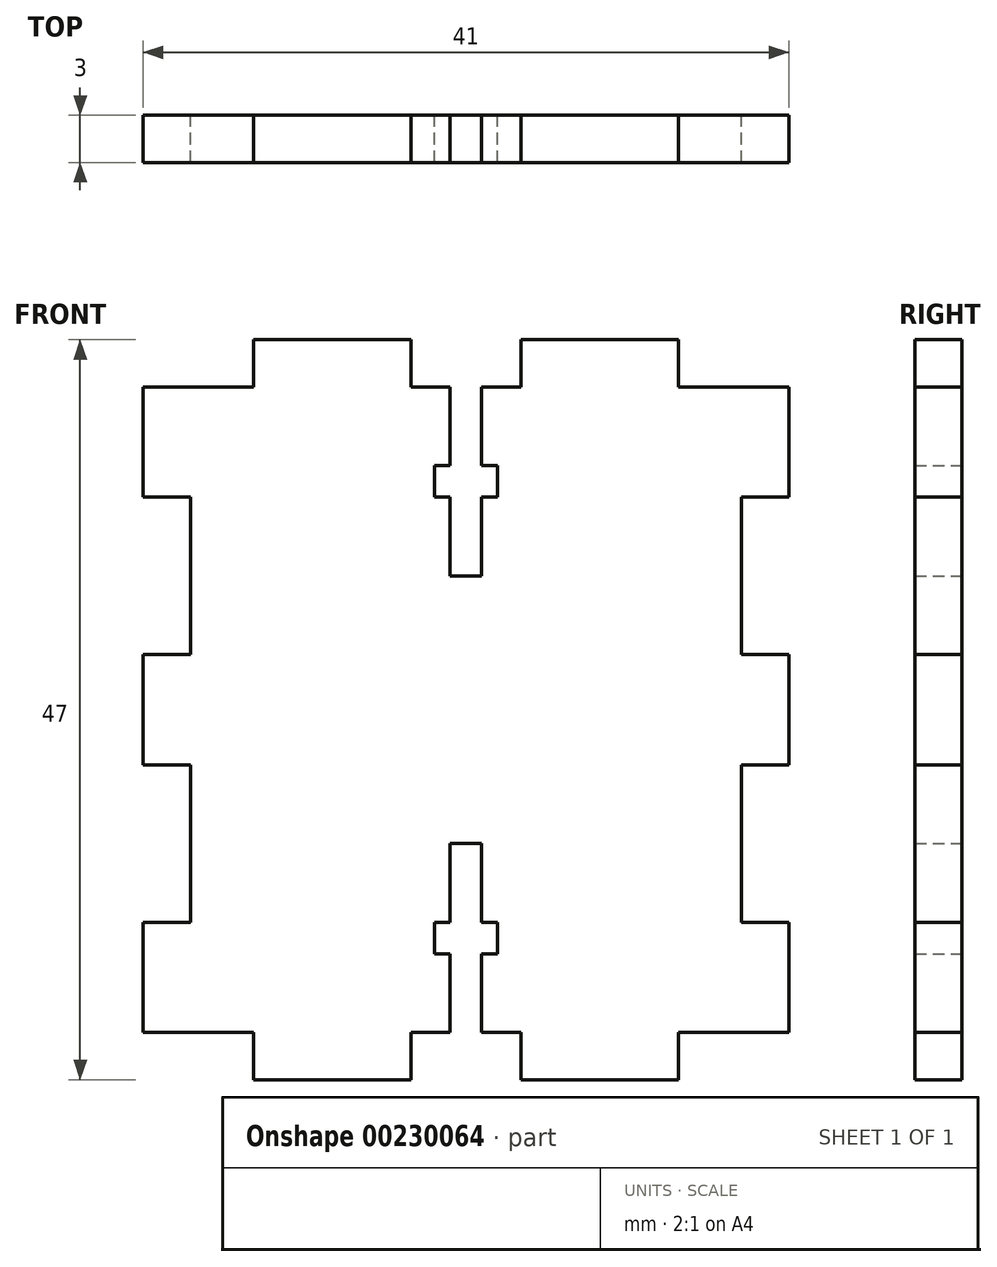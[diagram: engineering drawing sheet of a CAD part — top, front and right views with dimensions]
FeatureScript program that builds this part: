
annotation { "Feature Type Name" : "Feature", "Feature Type Description" : "" }
export const myFeature = defineFeature(function(context is Context, id is Id, definition is map)
    precondition{}
    {
        {
            var Q0;
            Q0=qCreatedBy(makeId("Front.planeOp"),FACE);
            var sketch = newSketch(context, id + "F0", { "sketchPlane" : qUnion([Q0])});
            skLineSegment(sketch, "E0", {"start": v(0, 0) * mm, "end": v(0, 3) * mm});
            skLineSegment(sketch, "E1", {"start": v(0, 3) * mm, "end": v(3, 3) * mm});
            skLineSegment(sketch, "E2", {"start": v(3, 3) * mm, "end": v(3, 10) * mm});
            skLineSegment(sketch, "E3", {"start": v(3, 10) * mm, "end": v(0, 10) * mm});
            skLineSegment(sketch, "E4", {"start": v(0, 10) * mm, "end": v(0, 20) * mm});
            skLineSegment(sketch, "E5", {"start": v(0, 20) * mm, "end": v(3, 20) * mm});
            skLineSegment(sketch, "E6", {"start": v(3, 20) * mm, "end": v(3, 27) * mm});
            skLineSegment(sketch, "E7", {"start": v(3, 27) * mm, "end": v(0, 27) * mm});
            skLineSegment(sketch, "E8", {"start": v(0, 27) * mm, "end": v(0, 37) * mm});
            skLineSegment(sketch, "E9", {"start": v(0, 37) * mm, "end": v(3, 37) * mm});
            skLineSegment(sketch, "E10", {"start": v(3, 37) * mm, "end": v(3, 44) * mm});
            skLineSegment(sketch, "E11", {"start": v(3, 44) * mm, "end": v(-4, 44) * mm});
            skLineSegment(sketch, "E12", {"start": v(-4, 44) * mm, "end": v(-4, 47) * mm});
            skLineSegment(sketch, "E13", {"start": v(-4, 47) * mm, "end": v(-14, 47) * mm});
            skLineSegment(sketch, "E14", {"start": v(-14, 47) * mm, "end": v(-14, 44) * mm});
            skLineSegment(sketch, "E15", {"start": v(-14, 44) * mm, "end": v(-16.5, 44) * mm});
            skLineSegment(sketch, "E16", {"start": v(-21, 44) * mm, "end": v(-21, 47) * mm});
            skLineSegment(sketch, "E17", {"start": v(-21, 47) * mm, "end": v(-31, 47) * mm});
            skLineSegment(sketch, "E18", {"start": v(-31, 47) * mm, "end": v(-31, 44) * mm});
            skLineSegment(sketch, "E19", {"start": v(-31, 44) * mm, "end": v(-38, 44) * mm});
            skLineSegment(sketch, "E20", {"start": v(3, 23.5) * mm, "end": v(-59.36, 23.5) * mm, "construction": true});
            skLineSegment(sketch, "E21", {"start": v(-17.5, 53.93) * mm, "end": v(-17.5, -3.72) * mm, "construction": true});
            skLineSegment(sketch, "E22.MirrorCS", {"start": v(-35, 0) * mm, "end": v(-35, 3) * mm});
            skLineSegment(sketch, "E23.MirrorCS", {"start": v(-35, 3) * mm, "end": v(-38, 3) * mm});
            skLineSegment(sketch, "E24.MirrorCS", {"start": v(-38, 3) * mm, "end": v(-38, 10) * mm});
            skLineSegment(sketch, "E25.MirrorCS", {"start": v(-38, 10) * mm, "end": v(-35, 10) * mm});
            skLineSegment(sketch, "E26.MirrorCS", {"start": v(-35, 20) * mm, "end": v(-38, 20) * mm});
            skLineSegment(sketch, "E27.MirrorCS", {"start": v(-38, 37) * mm, "end": v(-38, 44) * mm});
            skLineSegment(sketch, "E28.MirrorCS", {"start": v(-38, 20) * mm, "end": v(-38, 27) * mm});
            skLineSegment(sketch, "E29.MirrorCS", {"start": v(-38, 44) * mm, "end": v(-31, 44) * mm});
            skLineSegment(sketch, "E30.MirrorCS", {"start": v(-35, 37) * mm, "end": v(-38, 37) * mm});
            skLineSegment(sketch, "E31.MirrorCS", {"start": v(-35, 10) * mm, "end": v(-35, 20) * mm});
            skLineSegment(sketch, "E32.MirrorCS", {"start": v(-38, 27) * mm, "end": v(-35, 27) * mm});
            skLineSegment(sketch, "E33.MirrorCS", {"start": v(-35, 27) * mm, "end": v(-35, 37) * mm});
            skLineSegment(sketch, "E34.MirrorCS", {"start": v(-31, 3) * mm, "end": v(-38, 3) * mm});
            skLineSegment(sketch, "E35.MirrorCS", {"start": v(-21, 3) * mm, "end": v(-21, 0) * mm});
            skLineSegment(sketch, "E36.MirrorCS", {"start": v(-31, 0) * mm, "end": v(-31, 3) * mm});
            skLineSegment(sketch, "E37.MirrorCS", {"start": v(-38, 3) * mm, "end": v(-31, 3) * mm});
            skLineSegment(sketch, "E38.MirrorCS", {"start": v(-4, 3) * mm, "end": v(-4, 0) * mm});
            skLineSegment(sketch, "E39.MirrorCS", {"start": v(3, 3) * mm, "end": v(-4, 3) * mm});
            skLineSegment(sketch, "E40.MirrorCS", {"start": v(-14, 3) * mm, "end": v(-16.5, 3) * mm});
            skLineSegment(sketch, "E41.MirrorCS", {"start": v(-21, 0) * mm, "end": v(-31, 0) * mm});
            skLineSegment(sketch, "E42.MirrorCS", {"start": v(-4, 0) * mm, "end": v(-14, 0) * mm});
            skLineSegment(sketch, "E43.MirrorCS", {"start": v(-14, 0) * mm, "end": v(-14, 3) * mm});
            skLineSegment(sketch, "E44.top", {"start": v(-18.5, 32) * mm, "end": v(-16.5, 32) * mm});
            skLineSegment(sketch, "E44.left", {"start": v(-18.5, 44) * mm, "end": v(-18.5, 39) * mm});
            skLineSegment(sketch, "E44.right", {"start": v(-16.5, 44) * mm, "end": v(-16.5, 39) * mm});
            skLineSegment(sketch, "E45.trimOffspring", {"start": v(-18.5, 44) * mm, "end": v(-21, 44) * mm});
            skLineSegment(sketch, "E46.bottom", {"start": v(-19.5, 39) * mm, "end": v(-18.5, 39) * mm});
            skLineSegment(sketch, "E46.top", {"start": v(-19.5, 37) * mm, "end": v(-18.5, 37) * mm});
            skLineSegment(sketch, "E46.left", {"start": v(-19.5, 39) * mm, "end": v(-19.5, 37) * mm});
            skLineSegment(sketch, "E46.right", {"start": v(-15.5, 39) * mm, "end": v(-15.5, 37) * mm});
            skLineSegment(sketch, "E47.trimOffspring", {"start": v(-18.5, 37) * mm, "end": v(-18.5, 32) * mm});
            skLineSegment(sketch, "E48.trimOffspring", {"start": v(-16.5, 39) * mm, "end": v(-15.5, 39) * mm});
            skLineSegment(sketch, "E49.trimOffspring", {"start": v(-16.5, 37) * mm, "end": v(-16.5, 32) * mm});
            skLineSegment(sketch, "E50.trimOffspring", {"start": v(-16.5, 37) * mm, "end": v(-15.5, 37) * mm});
            skLineSegment(sketch, "E51.MirrorCS", {"start": v(-19.5, 10) * mm, "end": v(-18.5, 10) * mm});
            skLineSegment(sketch, "E52.MirrorCS", {"start": v(-16.5, 8) * mm, "end": v(-15.5, 8) * mm});
            skLineSegment(sketch, "E53.MirrorCS", {"start": v(-16.5, 10) * mm, "end": v(-15.5, 10) * mm});
            skLineSegment(sketch, "E54.MirrorCS", {"start": v(-19.5, 8) * mm, "end": v(-18.5, 8) * mm});
            skLineSegment(sketch, "E55.MirrorCS", {"start": v(-19.5, 8) * mm, "end": v(-19.5, 10) * mm});
            skLineSegment(sketch, "E56.MirrorCS", {"start": v(-16.5, 10) * mm, "end": v(-16.5, 15) * mm});
            skLineSegment(sketch, "E57.MirrorCS", {"start": v(-15.5, 8) * mm, "end": v(-15.5, 10) * mm});
            skLineSegment(sketch, "E58.MirrorCS", {"start": v(-16.5, 3) * mm, "end": v(-16.5, 8) * mm});
            skLineSegment(sketch, "E59.MirrorCS", {"start": v(-18.5, 3) * mm, "end": v(-18.5, 8) * mm});
            skLineSegment(sketch, "E60.MirrorCS", {"start": v(-18.5, 10) * mm, "end": v(-18.5, 15) * mm});
            skLineSegment(sketch, "E61.MirrorCS", {"start": v(-18.5, 15) * mm, "end": v(-16.5, 15) * mm});
            skLineSegment(sketch, "E62.trimOffspring", {"start": v(-18.5, 3) * mm, "end": v(-21, 3) * mm});
            skSolve(sketch);
        }
        {
            var Q0;
            Q0 = qSketchRegion(id + "F0", true);
            extrude(context, id + "F1", {"entities" : qUnion([Q0]), "depth" : 3 * mm});
        }
    });
